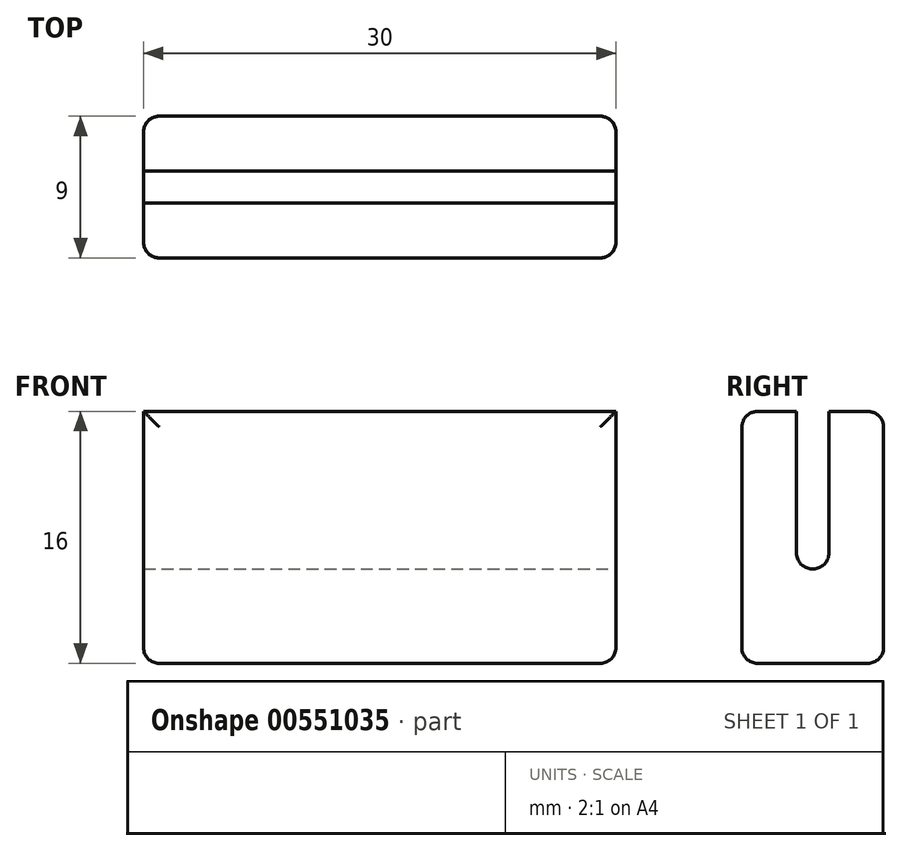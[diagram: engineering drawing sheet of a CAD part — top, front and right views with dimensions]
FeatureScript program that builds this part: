
annotation { "Feature Type Name" : "Feature", "Feature Type Description" : "" }
export const myFeature = defineFeature(function(context is Context, id is Id, definition is map)
    precondition{}
    {
        {
            var Q0;
            Q0=qCreatedBy(makeId("Top.planeOp"),FACE);
            var sketch = newSketch(context, id + "F0", { "sketchPlane" : qUnion([Q0])});
            skLineSegment(sketch, "E0.bottom", {"start": v(-15, -4.5) * mm, "end": v(15, -4.5) * mm});
            skLineSegment(sketch, "E0.top", {"start": v(-15, 4.5) * mm, "end": v(15, 4.5) * mm});
            skLineSegment(sketch, "E0.left", {"start": v(-15, -4.5) * mm, "end": v(-15, 4.5) * mm});
            skLineSegment(sketch, "E0.right", {"start": v(15, -4.5) * mm, "end": v(15, 4.5) * mm});
            skPoint(sketch, "E0.middle", {"position": v(0, 0) * mm});
            skSolve(sketch);
        }
        {
            var Q0;
            Q0 = qSketchRegion(id + "F0", true);
            extrude(context, id + "F1", {"entities" : qUnion([Q0]), "depth" : 16 * mm, "offsetDistance" : 25 * mm});
        }
        {
            var Q0;
            Q0=makeQuery(id+"F1.opExtrude","CAP_FACE",FACE,{"disambiguationData":[OSD([sQuery(id+"F0.wireOp",EDGE,"E0.bottom"),sQuery(id+"F0.wireOp",EDGE,"E0.top"),sQuery(id+"F0.wireOp",EDGE,"E0.left"),sQuery(id+"F0.wireOp",EDGE,"E0.right")])],"isStart":false});
            var sketch = newSketch(context, id + "F2", { "sketchPlane" : qUnion([Q0])});
            skLineSegment(sketch, "E1.bottom", {"start": v(-15, -1.03) * mm, "end": v(15, -1.03) * mm});
            skLineSegment(sketch, "E1.top", {"start": v(-15, 1.03) * mm, "end": v(15, 1.03) * mm});
            skLineSegment(sketch, "E1.left", {"start": v(-15, -1.03) * mm, "end": v(-15, 1.03) * mm});
            skLineSegment(sketch, "E1.right", {"start": v(15, -1.03) * mm, "end": v(15, 1.03) * mm});
            skPoint(sketch, "E1.middle", {"position": v(0, 0) * mm});
            skSolve(sketch);
        }
        {
            var Q0;
            Q0 = qSketchRegion(id + "F2", true);
            extrude(context, id + "F3", {"entities" : qUnion([Q0]), "operationType" : NewBodyOperationType.REMOVE, "oppositeDirection" : true, "depth" : 10 * mm, "offsetDistance" : 25 * mm});
        }
        {
            var Q0;
            Q0=makeQuery(id+"F3.boolean.opBoolean","COPY",EDGE,{"derivedFrom":makeQuery(id+"F3.opExtrude","CAP_EDGE",EDGE,{"disambiguationData":[OSD([sQuery(id+"F2.wireOp",EDGE,"E1.bottom")])],"isStart":false})});
            var Q1;
            Q1=makeQuery(id+"F3.boolean.opBoolean","COPY",EDGE,{"derivedFrom":makeQuery(id+"F3.opExtrude","CAP_EDGE",EDGE,{"disambiguationData":[OSD([sQuery(id+"F2.wireOp",EDGE,"E1.top")])],"isStart":false})});
            fillet(context, id + "F4", {"entities" : qUnion([Q0, Q1]), "radius" : 1 * mm, "tangentPropagation" : true, "allowEdgeOverflow" : false});
        }
        {
            var Q0;
            Q0=makeQuery(id+"F1.opExtrude","CAP_EDGE",EDGE,{"disambiguationData":[OSD([sQuery(id+"F0.wireOp",EDGE,"E0.top")])],"isStart":false});
            var Q1;
            Q1=makeQuery(id+"F1.opExtrude","CAP_EDGE",EDGE,{"disambiguationData":[OSD([sQuery(id+"F0.wireOp",EDGE,"E0.bottom")])],"isStart":false});
            var Q2;
            Q2=makeQuery(id+"F1.opExtrude","CAP_EDGE",EDGE,{"disambiguationData":[OSD([sQuery(id+"F0.wireOp",EDGE,"E0.top")])],"isStart":true});
            var Q3;
            Q3=makeQuery(id+"F1.opExtrude","CAP_EDGE",EDGE,{"disambiguationData":[OSD([sQuery(id+"F0.wireOp",EDGE,"E0.bottom")])],"isStart":true});
            var Q4;
            Q4=makeQuery(id+"F1.opExtrude","CAP_EDGE",EDGE,{"disambiguationData":[OSD([sQuery(id+"F0.wireOp",EDGE,"E0.right")])],"isStart":true});
            var Q5;
            Q5=makeQuery(id+"F1.opExtrude","SWEPT_EDGE",EDGE,{"disambiguationData":[OSD([sQuery(id+"F0.wireOp",EDGE,"E0.bottom"),sQuery(id+"F0.wireOp",EDGE,"E0.right")])]});
            var Q6;
            Q6=makeQuery(id+"F1.opExtrude","SWEPT_EDGE",EDGE,{"disambiguationData":[OSD([sQuery(id+"F0.wireOp",EDGE,"E0.top"),sQuery(id+"F0.wireOp",EDGE,"E0.right")])]});
            var Q7;
            Q7=makeQuery(id+"F1.opExtrude","SWEPT_EDGE",EDGE,{"disambiguationData":[OSD([sQuery(id+"F0.wireOp",EDGE,"E0.top"),sQuery(id+"F0.wireOp",EDGE,"E0.left")])]});
            var Q8;
            Q8=makeQuery(id+"F1.opExtrude","CAP_EDGE",EDGE,{"disambiguationData":[OSD([sQuery(id+"F0.wireOp",EDGE,"E0.left")])],"isStart":true});
            var Q9;
            Q9=makeQuery(id+"F1.opExtrude","SWEPT_EDGE",EDGE,{"disambiguationData":[OSD([sQuery(id+"F0.wireOp",EDGE,"E0.bottom"),sQuery(id+"F0.wireOp",EDGE,"E0.left")])]});
            fillet(context, id + "F5", {"entities" : qUnion([Q0, Q1, Q2, Q3, Q4, Q5, Q6, Q7, Q8, Q9]), "radius" : 1 * mm, "tangentPropagation" : true, "allowEdgeOverflow" : false});
        }
    });
